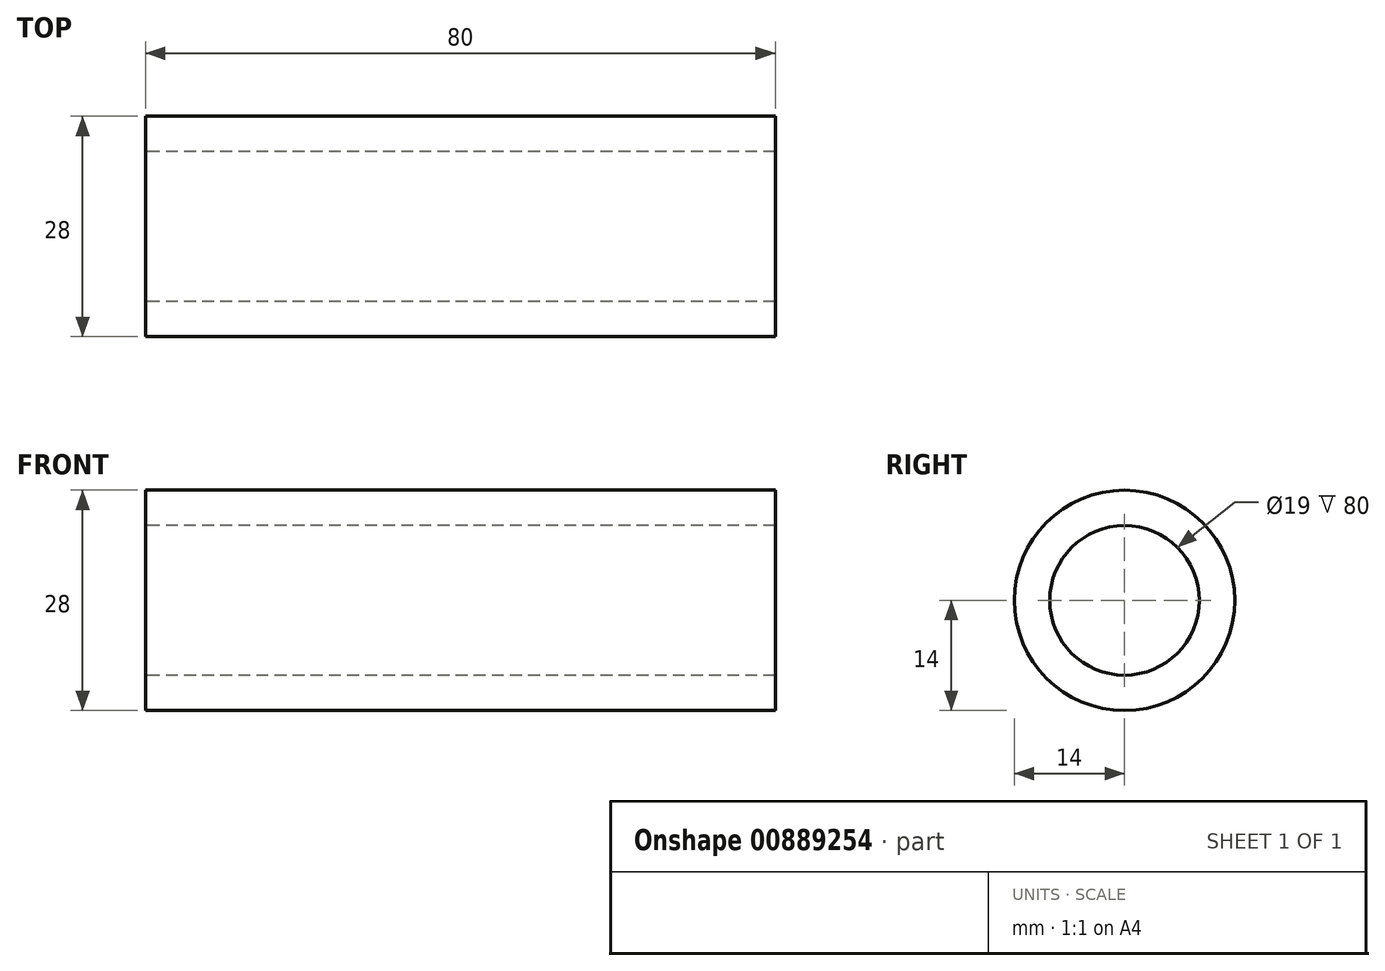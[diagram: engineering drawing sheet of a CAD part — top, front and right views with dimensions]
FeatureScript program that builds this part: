
annotation { "Feature Type Name" : "Feature", "Feature Type Description" : "" }
export const myFeature = defineFeature(function(context is Context, id is Id, definition is map)
    precondition{}
    {
        {
            var Q0;
            Q0=qCreatedBy(makeId("Front.planeOp"),FACE);
            var sketch = newSketch(context, id + "F0", { "sketchPlane" : qUnion([Q0])});
            skLineSegment(sketch, "E0", {"start": v(0, 14) * mm, "end": v(80, 14) * mm});
            skLineSegment(sketch, "E1", {"start": v(0, 9.5) * mm, "end": v(80, 9.5) * mm});
            skLineSegment(sketch, "E2", {"start": v(0, 14) * mm, "end": v(0, 9.5) * mm});
            skLineSegment(sketch, "E3", {"start": v(80, 14) * mm, "end": v(80, 9.17) * mm});
            skLineSegment(sketch, "E4", {"start": v(0, 0) * mm, "end": v(80, 0) * mm});
            skSolve(sketch);
        }
        {
            var Q0;
            {var subQ0=sQuery(id+"F0.wireOp",EDGE,"E0");Q0=makeQuery(id+"F0.imprint","IMPRINT",FACE,{"disambiguationData":[TD([[makeQuery(id+"F0.imprint","IMPRINT",EDGE,{"derivedFrom":subQ0}),-1.0]])]});}
            var Q1;
            Q1=sQuery(id+"F0.wireOp",EDGE,"E4");
            revolve(context, id + "F1", {"surfaceOperationType" : NewSurfaceOperationType.NEW, "entities" : qUnion([Q0]), "axis" : qUnion([Q1]), "revolveType" : RevolveType.FULL});
        }
    });
